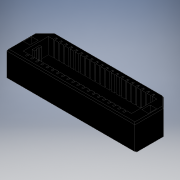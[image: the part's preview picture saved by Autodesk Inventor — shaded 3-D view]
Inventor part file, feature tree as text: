
AUTODESK INVENTOR PART (.ipt)
format: ipt  version: 2019 (Build 230136000, 136)  size: 357,376 bytes
history: native  units: in
note: dims shown in document units (in); Inventor stores cm internally (conversion verified against a paired STEP export)
features: other x28, extrude x9, sketch x9
ambient origin geometry x8: Origin, YZ Plane, XZ Plane, XY Plane, X Axis, Y Axis, Z Axis, Center Point
bodies: Solid1 (feature_tree)
feature tree (46):
  extrude  "Extrusion1"  Depth=0.01in
  extrude  "Extrusion2"  Depth=0.32in TaperAngle=0.0deg
  extrude  "Extrusion3"  Depth=0.078in TaperAngle=0.0deg
  extrude  "Extrusion4"  Depth=0.011in TaperAngle=0.0deg
  extrude  "Extrusion5"  TaperAngle=0.0deg  [1 undecoded]
  extrude  "Extrusion6"  [1 undecoded]
  extrude  "Extrusion7"  [1 undecoded]
  extrude  "Extrusion8"  [1 undecoded]
  extrude  "Extrusion9"  [1 undecoded]
  other  "metal_plane_1_XY"
  other  "metal_plane_1_YZ"
  other  "metal_plane_1_ZX"
  other  "metal_plane_1_X"
  other  "metal_plane_1_Y"
  other  "metal_plane_1_Z"
  other  "metal_plane_1_Center"
  other  "pad_1_XY"
  other  "pad_1_YZ"
  other  "pad_1_ZX"
  other  "pad_1_X"
  other  "pad_1_Y"
  other  "pad_1_Z"
  other  "pad_1_Center"
  other  "pin_left_1_XY"
  other  "pin_left_1_YZ"
  other  "pin_left_1_ZX"
  other  "pin_left_1_X"
  other  "pin_left_1_Y"
  other  "pin_left_1_Z"
  other  "pin_left_1_Center"
  other  "terminal_XY"
  other  "terminal_YZ"
  other  "terminal_ZX"
  other  "terminal_X"
  other  "terminal_Y"
  other  "terminal_Z"
  other  "terminal_Center"
  sketch  "Sketch_1"  dims[d0=0.15in d1=0.0in d2=0.01in d3=-0.2128in]
  sketch  "Sketch_7"  dims[d4=0.196in d5=0.0in d6=0.32in d7=0.0in]
  sketch  "Sketch_16"  dims[d8=0.32in d9=0.0in d10=0.078in d11=0.0in]
  sketch  "Sketch_32"  dims[d12=0.078in d13=0.0in d14=0.011in d15=0.0in]
  sketch  "Sketch_33"  dims[d16=1.776in d17=0.0in d18=0.0in d19=0.0in]
  sketch  "Sketch_34"
  sketch  "Sketch_35"
  sketch  "Sketch_44"
  sketch  "Sketch_54"
note: 5 required parameter values undecoded (feature->parameter linkage not recoverable at this tier; creation-order binding heuristic only, values carry confidence <= 0.55)
